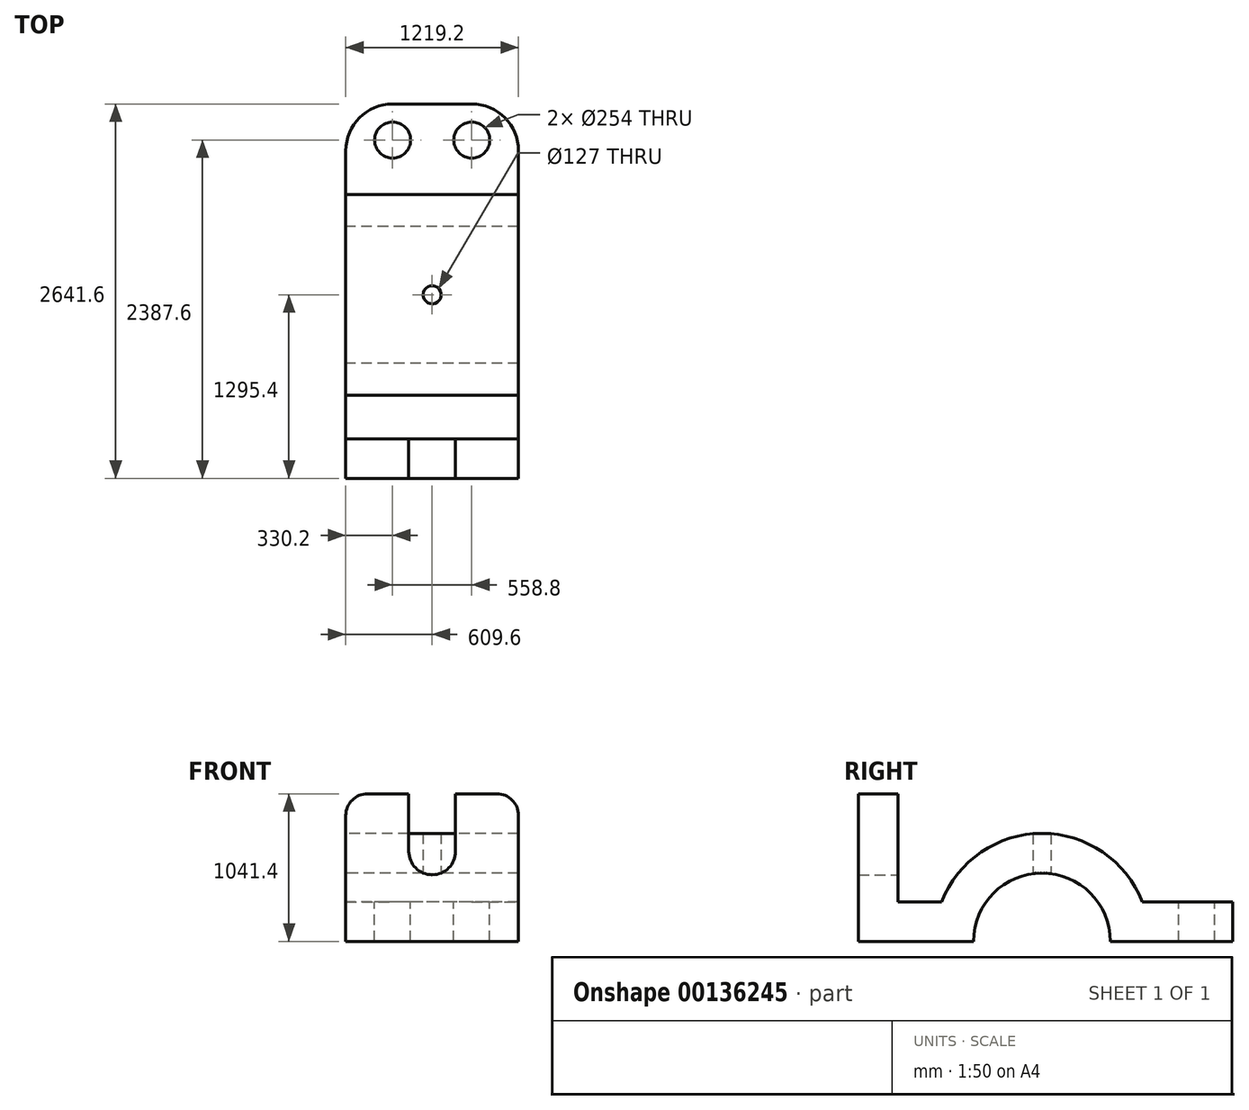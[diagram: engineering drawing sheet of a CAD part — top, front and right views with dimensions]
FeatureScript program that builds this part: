
annotation { "Feature Type Name" : "Feature", "Feature Type Description" : "" }
export const myFeature = defineFeature(function(context is Context, id is Id, definition is map)
    precondition{}
    {
        {
            var Q0;
            Q0=qCreatedBy(makeId("Front.planeOp"),FACE);
            var sketch = newSketch(context, id + "F0", { "sketchPlane" : qUnion([Q0])});
            skLineSegment(sketch, "E0", {"start": v(0, 0) * mm, "end": v(609.6, 0) * mm});
            skLineSegment(sketch, "E1", {"start": v(0, 0) * mm, "end": v(-609.6, 0) * mm});
            skLineSegment(sketch, "E2", {"start": v(-609.6, 0) * mm, "end": v(-609.6, 889) * mm});
            skLineSegment(sketch, "E3", {"start": v(609.6, 0) * mm, "end": v(609.6, 889) * mm});
            skArc(sketch, "E4", {"start": v(-165.1, 635) * mm, "mid": v(0, 469.9) * mm, "end": v(165.1, 635) * mm});
            skLineSegment(sketch, "E5", {"start": v(165.1, 635) * mm, "end": v(165.1, 1041.4) * mm});
            skLineSegment(sketch, "E6", {"start": v(165.1, 1041.4) * mm, "end": v(457.2, 1041.4) * mm});
            skLineSegment(sketch, "E7", {"start": v(-165.1, 635) * mm, "end": v(-165.1, 1041.4) * mm});
            skLineSegment(sketch, "E8", {"start": v(-165.1, 1041.4) * mm, "end": v(-457.2, 1041.4) * mm});
            skPoint(sketch, "E9.visualSharp", {"position": v(-609.6, 1041.4) * mm});
            skArc(sketch, "E9.filletArc", {"start": v(-457.2, 1041.4) * mm, "mid": v(-564.96, 996.76) * mm, "end": v(-609.6, 889) * mm});
            skPoint(sketch, "E10.visualSharp", {"position": v(609.6, 1041.4) * mm});
            skArc(sketch, "E10.filletArc", {"start": v(609.6, 889) * mm, "mid": v(564.96, 996.76) * mm, "end": v(457.2, 1041.4) * mm});
            skSolve(sketch);
        }
        {
            var Q0;
            Q0 = qSketchRegion(id + "F0", true);
            extrude(context, id + "F1", {"entities" : qUnion([Q0]), "depth" : 279.4 * mm});
        }
        {
            var Q0;
            Q0=qCreatedBy(makeId("Right.planeOp"),FACE);
            var sketch = newSketch(context, id + "F2", { "sketchPlane" : qUnion([Q0])});
            skLineSegment(sketch, "E11", {"start": v(0, 0) * mm, "end": v(533.78, 0) * mm});
            skArc(sketch, "E12", {"start": v(1498.22, 0) * mm, "mid": v(1016, 482.22) * mm, "end": v(533.78, 0) * mm});
            skArc(sketch, "E13", {"start": v(1724.93, 279.4) * mm, "mid": v(1016, 762) * mm, "end": v(307.07, 279.4) * mm});
            skLineSegment(sketch, "E14", {"start": v(2362.2, 0) * mm, "end": v(2362.2, 279.4) * mm});
            skLineSegment(sketch, "E15", {"start": v(2362.2, 279.4) * mm, "end": v(1724.93, 279.4) * mm});
            skLineSegment(sketch, "E16.trimOffspring", {"start": v(307.07, 279.4) * mm, "end": v(0, 279.4) * mm});
            skLineSegment(sketch, "E17.trimOffspring", {"start": v(1498.22, 0) * mm, "end": v(2362.2, 0) * mm});
            skLineSegment(sketch, "E18", {"start": v(0, 279.4) * mm, "end": v(0, 0) * mm});
            skSolve(sketch);
        }
        {
            var Q0;
            Q0 = qSketchRegion(id + "F2", true);
            extrude(context, id + "F3", {"entities" : qUnion([Q0]), "operationType" : NewBodyOperationType.ADD, "endBound" : BoundingType.SYMMETRIC, "depth" : 1219.2 * mm});
        }
        {
            var Q0;
            Q0=makeQuery(id+"F3.opExtrude","SWEPT_FACE",FACE,{"disambiguationData":[OSD([sQuery(id+"F2.wireOp",EDGE,"E15")])]});
            var sketch = newSketch(context, id + "F4", { "sketchPlane" : qUnion([Q0])});
            skPoint(sketch, "E19.endSnap0", {"position": v(0, 1724.93) * mm});
            skCircle(sketch, "E20", {"center": v(279.4, 2108.2) * mm, "radius": 127 * mm});
            skCircle(sketch, "E21", {"center": v(-279.4, 2108.2) * mm, "radius": 127 * mm});
            skLineSegment(sketch, "E22", {"start": v(0, 0) * mm, "end": v(0, 1016) * mm});
            skCircle(sketch, "E23", {"center": v(0, 1016) * mm, "radius": 63.5 * mm});
            skSolve(sketch);
        }
        {
            var Q0;
            Q0 = qSketchRegion(id + "F4", true);
            extrude(context, id + "F5", {"entities" : qUnion([Q0]), "operationType" : NewBodyOperationType.REMOVE, "endBound" : BoundingType.THROUGH_ALL, "oppositeDirection" : true, "depth" : 25.4 * mm});
        }
        {
            var Q0;
            Q0 = qSketchRegion(id + "F4", true);
            extrude(context, id + "F6", {"entities" : qUnion([Q0]), "operationType" : NewBodyOperationType.REMOVE, "endBound" : BoundingType.THROUGH_ALL, "depth" : 25.4 * mm});
        }
        {
            var Q0;
            Q0=makeQuery(id+"F3.opExtrude","CAP_EDGE",EDGE,{"disambiguationData":[OSD([sQuery(id+"F2.wireOp",EDGE,"E14")])],"isStart":true});
            var Q1;
            Q1=makeQuery(id+"F3.opExtrude","CAP_EDGE",EDGE,{"disambiguationData":[OSD([sQuery(id+"F2.wireOp",EDGE,"E14")])],"isStart":false});
            fillet(context, id + "F7", {"entities" : qUnion([Q0, Q1]), "radius" : 330.2 * mm, "tangentPropagation" : true, "allowEdgeOverflow" : false});
        }
    });
